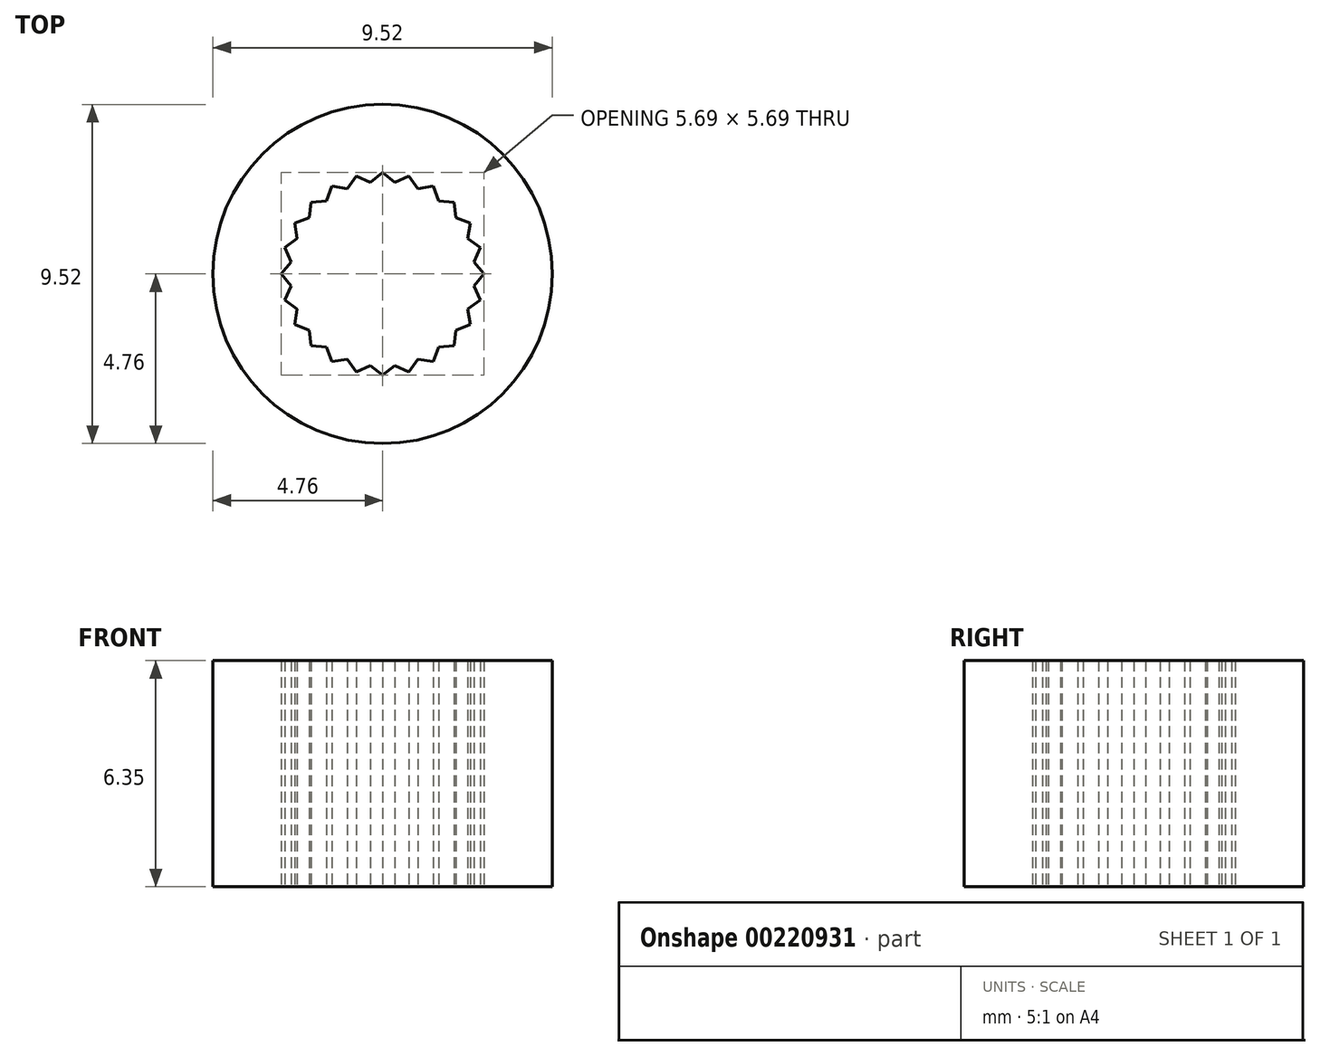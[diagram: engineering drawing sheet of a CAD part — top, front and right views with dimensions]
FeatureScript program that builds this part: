
annotation { "Feature Type Name" : "Feature", "Feature Type Description" : "" }
export const myFeature = defineFeature(function(context is Context, id is Id, definition is map)
    precondition{}
    {
        {
            var Q0;
            Q0=qCreatedBy(makeId("Top.planeOp"),FACE);
            var sketch = newSketch(context, id + "F0", { "sketchPlane" : qUnion([Q0])});
            skCircle(sketch, "E0", {"center": v(0, 0) * mm, "radius": 2.84 * mm, "construction": true});
            skCircle(sketch, "E1", {"center": v(0, 0) * mm, "radius": 2.6 * mm, "construction": true});
            skCircle(sketch, "E2", {"center": v(0, 0) * mm, "radius": 4.76 * mm});
            skLineSegment(sketch, "E3", {"start": v(-0.34, 2.57) * mm, "end": v(0, 2.84) * mm});
            skLineSegment(sketch, "E4", {"start": v(0, 2.84) * mm, "end": v(0.34, 2.57) * mm});
            skLineSegment(sketch, "E5", {"start": v(0.34, 2.57) * mm, "end": v(0.74, 2.75) * mm});
            skLineSegment(sketch, "E6", {"start": v(0.74, 2.75) * mm, "end": v(1, 2.4) * mm});
            skLineSegment(sketch, "E7", {"start": v(1, 2.4) * mm, "end": v(1.42, 2.46) * mm});
            skLineSegment(sketch, "E8", {"start": v(1.42, 2.46) * mm, "end": v(1.58, 2.06) * mm});
            skLineSegment(sketch, "E9", {"start": v(1.58, 2.06) * mm, "end": v(2.01, 2.01) * mm});
            skLineSegment(sketch, "E10", {"start": v(2.01, 2.01) * mm, "end": v(2.06, 1.58) * mm});
            skLineSegment(sketch, "E11", {"start": v(2.06, 1.58) * mm, "end": v(2.46, 1.42) * mm});
            skLineSegment(sketch, "E12", {"start": v(2.46, 1.42) * mm, "end": v(2.4, 1) * mm});
            skLineSegment(sketch, "E13", {"start": v(2.4, 1) * mm, "end": v(2.75, 0.74) * mm});
            skLineSegment(sketch, "E14", {"start": v(2.75, 0.74) * mm, "end": v(2.57, 0.34) * mm});
            skLineSegment(sketch, "E15", {"start": v(2.57, 0.34) * mm, "end": v(2.84, 0) * mm});
            skLineSegment(sketch, "E16", {"start": v(2.84, 0) * mm, "end": v(2.57, -0.34) * mm});
            skLineSegment(sketch, "E17", {"start": v(2.57, -0.34) * mm, "end": v(2.75, -0.74) * mm});
            skLineSegment(sketch, "E18", {"start": v(2.75, -0.74) * mm, "end": v(2.4, -1) * mm});
            skLineSegment(sketch, "E19", {"start": v(2.4, -1) * mm, "end": v(2.46, -1.42) * mm});
            skLineSegment(sketch, "E20", {"start": v(2.46, -1.42) * mm, "end": v(2.06, -1.58) * mm});
            skLineSegment(sketch, "E21", {"start": v(2.06, -1.58) * mm, "end": v(2.01, -2.01) * mm});
            skLineSegment(sketch, "E22", {"start": v(2.01, -2.01) * mm, "end": v(1.58, -2.06) * mm});
            skLineSegment(sketch, "E23", {"start": v(1.58, -2.06) * mm, "end": v(1.42, -2.46) * mm});
            skLineSegment(sketch, "E24", {"start": v(1.42, -2.46) * mm, "end": v(1, -2.4) * mm});
            skLineSegment(sketch, "E25", {"start": v(1, -2.4) * mm, "end": v(0.74, -2.75) * mm});
            skLineSegment(sketch, "E26", {"start": v(0.74, -2.75) * mm, "end": v(0.34, -2.57) * mm});
            skLineSegment(sketch, "E27", {"start": v(0.34, -2.57) * mm, "end": v(0, -2.84) * mm});
            skLineSegment(sketch, "E28", {"start": v(0, -2.84) * mm, "end": v(-0.34, -2.57) * mm});
            skLineSegment(sketch, "E29", {"start": v(-0.34, 2.57) * mm, "end": v(-0.74, 2.75) * mm});
            skLineSegment(sketch, "E30", {"start": v(-0.74, 2.75) * mm, "end": v(-1, 2.4) * mm});
            skLineSegment(sketch, "E31", {"start": v(-1, 2.4) * mm, "end": v(-1.42, 2.46) * mm});
            skLineSegment(sketch, "E32", {"start": v(-1.42, 2.46) * mm, "end": v(-1.58, 2.06) * mm});
            skLineSegment(sketch, "E33", {"start": v(-1.58, 2.06) * mm, "end": v(-2.01, 2.01) * mm});
            skLineSegment(sketch, "E34", {"start": v(-2.01, 2.01) * mm, "end": v(-2.06, 1.58) * mm});
            skLineSegment(sketch, "E35", {"start": v(-2.06, 1.58) * mm, "end": v(-2.46, 1.42) * mm});
            skLineSegment(sketch, "E36", {"start": v(-2.46, 1.42) * mm, "end": v(-2.4, 1) * mm});
            skLineSegment(sketch, "E37", {"start": v(-2.4, 1) * mm, "end": v(-2.75, 0.74) * mm});
            skLineSegment(sketch, "E38", {"start": v(-2.75, 0.74) * mm, "end": v(-2.57, 0.34) * mm});
            skLineSegment(sketch, "E39", {"start": v(-2.57, 0.34) * mm, "end": v(-2.84, 0) * mm});
            skLineSegment(sketch, "E40", {"start": v(-2.84, 0) * mm, "end": v(-2.57, -0.34) * mm});
            skLineSegment(sketch, "E41", {"start": v(-2.57, -0.34) * mm, "end": v(-2.75, -0.74) * mm});
            skLineSegment(sketch, "E42", {"start": v(-2.75, -0.74) * mm, "end": v(-2.4, -1) * mm});
            skLineSegment(sketch, "E43", {"start": v(-2.4, -1) * mm, "end": v(-2.46, -1.42) * mm});
            skLineSegment(sketch, "E44", {"start": v(-2.46, -1.42) * mm, "end": v(-2.06, -1.58) * mm});
            skLineSegment(sketch, "E45", {"start": v(-2.06, -1.58) * mm, "end": v(-2.01, -2.01) * mm});
            skLineSegment(sketch, "E46", {"start": v(-2.01, -2.01) * mm, "end": v(-1.58, -2.06) * mm});
            skLineSegment(sketch, "E47", {"start": v(-1.58, -2.06) * mm, "end": v(-1.42, -2.46) * mm});
            skLineSegment(sketch, "E48", {"start": v(-1.42, -2.46) * mm, "end": v(-1, -2.4) * mm});
            skLineSegment(sketch, "E49", {"start": v(-1, -2.4) * mm, "end": v(-0.74, -2.75) * mm});
            skLineSegment(sketch, "E50", {"start": v(-0.74, -2.75) * mm, "end": v(-0.34, -2.57) * mm});
            skLineSegment(sketch, "E51", {"start": v(-4.12, 2.38) * mm, "end": v(9.17, 25.4) * mm});
            skLineSegment(sketch, "E52", {"start": v(9.17, 25.4) * mm, "end": v(28.22, 25.4) * mm});
            skLineSegment(sketch, "E53", {"start": v(4.12, -2.38) * mm, "end": v(16.5, 19.05) * mm});
            skLineSegment(sketch, "E54", {"start": v(16.5, 19.05) * mm, "end": v(28.22, 19.05) * mm});
            skArc(sketch, "E55", {"start": v(53.62, 0) * mm, "mid": v(46.18, 17.96) * mm, "end": v(28.22, 25.4) * mm});
            skArc(sketch, "E56", {"start": v(47.27, 0) * mm, "mid": v(41.69, 13.47) * mm, "end": v(28.22, 19.05) * mm});
            skArc(sketch, "E57", {"start": v(46.93, 3.57) * mm, "mid": v(50.25, 0.53) * mm, "end": v(53.33, 3.81) * mm});
            skSolve(sketch);
        }
        {
            var Q0;
            Q0=makeQuery(id+"F0.imprint","IMPRINT",FACE,{"disambiguationData":[TD([[makeQuery(id+"F0.imprint","IMPRINT",EDGE,{"derivedFrom":sQuery(id+"F0.wireOp",EDGE,"E2")}),1.0]])]});
            extrude(context, id + "F1", {"entities" : qUnion([Q0]), "depth" : 6.35 * mm});
        }
    });
